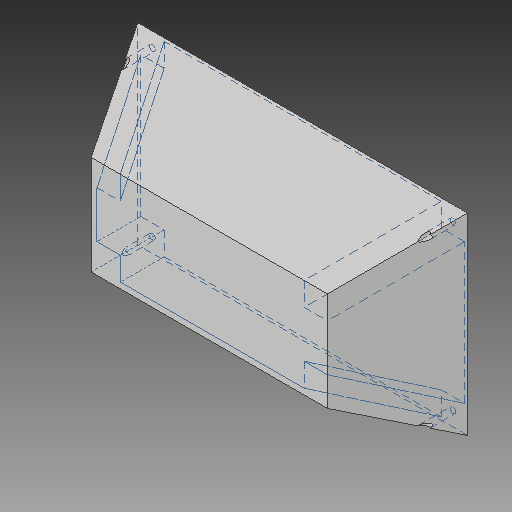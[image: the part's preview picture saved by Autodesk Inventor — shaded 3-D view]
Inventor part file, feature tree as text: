
AUTODESK INVENTOR PART (.ipt)
format: ipt  version: 2019 (Build 230136000, 136)  size: 159,744 bytes
history: native  units: in
note: dims shown in document units (in); Inventor stores cm internally (conversion verified against a paired STEP export)
features: sketch x5, plane x2, loft x2, extrude x1
ambient origin geometry x8: Origin, YZ Plane, XZ Plane, XY Plane, X Axis, Y Axis, Z Axis, Center Point
bodies: Solid1 (feature_tree)
feature tree (10):
  sketch  "Sketch1"  dims[d0=14.125in d1=8.25in]
  plane  "Work Plane1"
  loft  "Loft1"
  sketch  "Sketch3"  dims[d4=2.0in d5=0.0in d6=90.0deg]
  plane  "Work Plane2"
  loft  "Loft2"
  extrude  "Extrusion1"  TaperAngle=0.0deg  [1 undecoded]
  sketch  "Sketch2"  dims[d2=4.0in d3=2.0in]
  sketch  "Sketch5"  dims[d7=0.0in d8=90.0deg]
  sketch  "Sketch6"  dims[d9=0.125in d10=0.125in d11=1.0in d12=3.875in d15=0.125in d16=0.0in d17=90.0deg d18=0.0in d19=90.0deg d20=0.5in d21=0.5in d22=0.25in d23=1.0in d24=0.0in]
note: 1 required parameter value undecoded (feature->parameter linkage not recoverable at this tier; creation-order binding heuristic only, values carry confidence <= 0.55)
